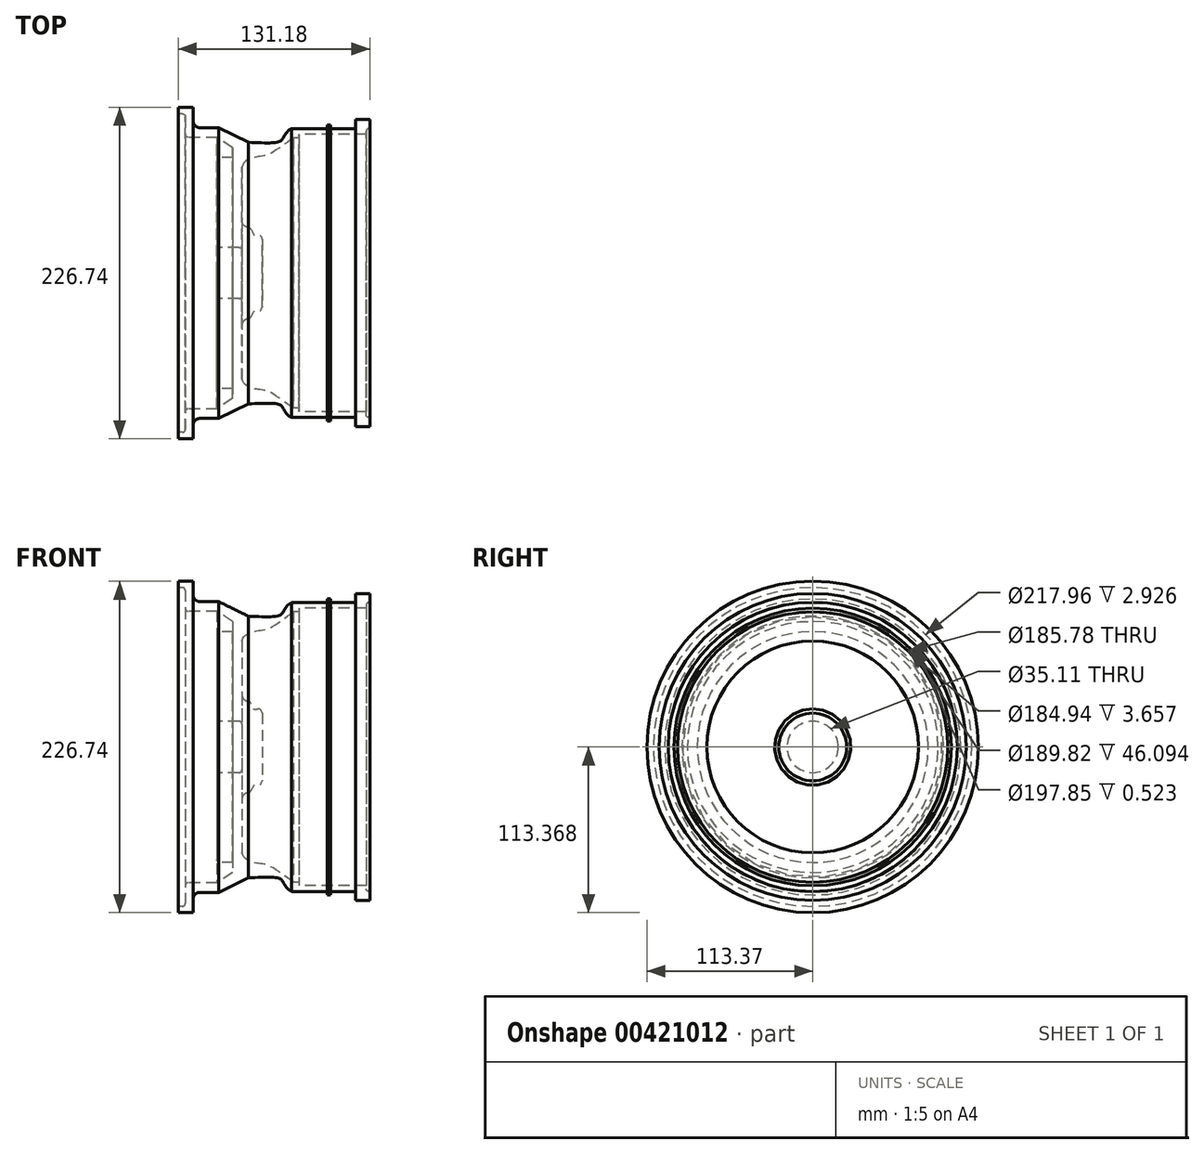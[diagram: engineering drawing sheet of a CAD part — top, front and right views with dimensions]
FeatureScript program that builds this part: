
annotation { "Feature Type Name" : "Feature", "Feature Type Description" : "" }
export const myFeature = defineFeature(function(context is Context, id is Id, definition is map)
    precondition{}
    {
        {
            var Q0;
            Q0=qCreatedBy(makeId("Front.planeOp"),FACE);
            var sketch = newSketch(context, id + "F0", { "sketchPlane" : qUnion([Q0])});
            skLineSegment(sketch, "E0", {"start": v(-61.95, 63.46) * mm, "end": v(-61.95, 59.07) * mm});
            skLineSegment(sketch, "E1", {"start": v(-61.95, 59.07) * mm, "end": v(-59.03, 59.07) * mm});
            skLineSegment(sketch, "E2", {"start": v(-57.07, 57.12) * mm, "end": v(-57.07, 44.93) * mm});
            skPoint(sketch, "E3.visualSharp", {"position": v(-57.07, 59.07) * mm});
            skArc(sketch, "E3.filletArc", {"start": v(-57.07, 57.12) * mm, "mid": v(-57.65, 58.5) * mm, "end": v(-59.03, 59.07) * mm});
            skLineSegment(sketch, "E4", {"start": v(-55.12, 42.98) * mm, "end": v(-35.38, 42.98) * mm});
            skPoint(sketch, "E5.visualSharp", {"position": v(-57.07, 42.98) * mm});
            skArc(sketch, "E5.filletArc", {"start": v(-57.07, 44.93) * mm, "mid": v(-56.5, 43.55) * mm, "end": v(-55.12, 42.98) * mm});
            skLineSegment(sketch, "E6", {"start": v(-35.38, 42.98) * mm, "end": v(-24.65, 35.9) * mm});
            skLineSegment(sketch, "E7", {"start": v(-24.65, 35.9) * mm, "end": v(-24.65, 29.08) * mm});
            skLineSegment(sketch, "E8", {"start": v(-24.65, 29.08) * mm, "end": v(-33.43, 29.08) * mm});
            skLineSegment(sketch, "E9", {"start": v(-35.38, 27.13) * mm, "end": v(-35.38, -32.36) * mm});
            skLineSegment(sketch, "E10", {"start": v(-35.38, -32.36) * mm, "end": v(-20.26, -32.36) * mm});
            skLineSegment(sketch, "E11", {"start": v(-18.3, -34.3) * mm, "end": v(-18.3, -49.91) * mm});
            skLineSegment(sketch, "E12", {"start": v(-18.3, -49.91) * mm, "end": v(-4.52, -49.91) * mm});
            skLineSegment(sketch, "E13", {"start": v(-4.52, -49.91) * mm, "end": v(-4.52, -26.75) * mm});
            skPoint(sketch, "E14.visualSharp", {"position": v(-35.38, 29.08) * mm});
            skArc(sketch, "E14.filletArc", {"start": v(-33.43, 29.08) * mm, "mid": v(-34.8, 28.5) * mm, "end": v(-35.38, 27.13) * mm});
            skPoint(sketch, "E15.visualSharp", {"position": v(-18.3, -32.36) * mm});
            skArc(sketch, "E15.filletArc", {"start": v(-18.3, -34.3) * mm, "mid": v(-18.88, -32.93) * mm, "end": v(-20.26, -32.36) * mm});
            skFitSpline(sketch, "E16", {"points": [v(-4.52, -26.75) * mm, v(-6.6, -23.82) * mm, v(-9.53, -24.31) * mm, v(-12.46, -19.44) * mm, v(-18.3, -18.95) * mm], "startDerivative": vector(-6.91, 20.58) * mm, "endDerivative": vector(-29.24, -4.58) * mm});
            skLineSegment(sketch, "E17", {"start": v(-18.3, -14.09) * mm, "end": v(-18.3, 22.5) * mm});
            skArc(sketch, "E18.filletArc", {"start": v(-18.3, -14.09) * mm, "mid": v(-17.16, -17.09) * mm, "end": v(-14.3, -18.55) * mm});
            skFitSpline(sketch, "E19", {"points": [v(-18.3, 22.5) * mm, v(-16.36, 26.16) * mm, v(-8.07, 29.57) * mm, v(0, 31.28) * mm, v(17, 42.56) * mm], "startDerivative": vector(6.68, 22.89) * mm, "endDerivative": vector(47.85, 31.3) * mm});
            skLineSegment(sketch, "E20", {"start": v(17, 42.56) * mm, "end": v(20.66, 42.56) * mm});
            skLineSegment(sketch, "E21", {"start": v(20.66, 42.56) * mm, "end": v(20.66, 45) * mm});
            skLineSegment(sketch, "E22", {"start": v(20.66, 45) * mm, "end": v(66.75, 45) * mm});
            skLineSegment(sketch, "E23", {"start": v(66.75, 45) * mm, "end": v(66.75, 47.06) * mm});
            skLineSegment(sketch, "E24", {"start": v(68.7, 49.01) * mm, "end": v(69.23, 49.01) * mm});
            skLineSegment(sketch, "E25", {"start": v(69.23, 49.01) * mm, "end": v(69.23, 55.07) * mm});
            skLineSegment(sketch, "E26", {"start": v(69.23, 55.07) * mm, "end": v(59.32, 55.07) * mm});
            skLineSegment(sketch, "E27", {"start": v(59.32, 55.07) * mm, "end": v(59.32, 48.9) * mm});
            skLineSegment(sketch, "E28", {"start": v(59.32, 48.9) * mm, "end": v(42.2, 48.9) * mm});
            skLineSegment(sketch, "E29", {"start": v(42.2, 48.9) * mm, "end": v(42.2, 51.35) * mm});
            skLineSegment(sketch, "E30", {"start": v(42.2, 51.35) * mm, "end": v(40.16, 51.35) * mm});
            skLineSegment(sketch, "E31", {"start": v(40.16, 51.35) * mm, "end": v(40.16, 48.9) * mm});
            skLineSegment(sketch, "E32", {"start": v(40.16, 48.9) * mm, "end": v(15.53, 48.9) * mm});
            skFitSpline(sketch, "E33", {"points": [v(15.53, 48.9) * mm, v(10.46, 43.47) * mm, v(7.29, 40.05) * mm, v(-13.9, 39.56) * mm], "startDerivative": vector(-23.57, -8.95) * mm, "endDerivative": vector(-53.39, 2.2) * mm});
            skLineSegment(sketch, "E34", {"start": v(-13.9, 39.56) * mm, "end": v(-34.37, 49.56) * mm});
            skLineSegment(sketch, "E35", {"start": v(-34.37, 49.56) * mm, "end": v(-47.2, 49.56) * mm});
            skLineSegment(sketch, "E36", {"start": v(-51.69, 54.05) * mm, "end": v(-51.69, 63.46) * mm});
            skLineSegment(sketch, "E37", {"start": v(-51.69, 63.46) * mm, "end": v(-61.95, 63.46) * mm});
            skPoint(sketch, "E38.visualSharp", {"position": v(-51.69, 49.56) * mm});
            skArc(sketch, "E38.filletArc", {"start": v(-51.69, 54.05) * mm, "mid": v(-50.37, 50.87) * mm, "end": v(-47.2, 49.56) * mm});
            skPoint(sketch, "E39.visualSharp", {"position": v(66.75, 49.01) * mm});
            skArc(sketch, "E39.filletArc", {"start": v(68.7, 49.01) * mm, "mid": v(67.32, 48.44) * mm, "end": v(66.75, 47.06) * mm});
            skSolve(sketch);
        }
        {
            var Q0;
            Q0=makeQuery(id+"F0.imprint","IMPRINT",FACE,{"disambiguationData":[TD([[makeQuery(id+"F0.imprint","IMPRINT",EDGE,{"derivedFrom":sQuery(id+"F0.wireOp",EDGE,"E0")}),1.0]])]});
            var Q1;
            Q1=sQuery(id+"F0.wireOp",EDGE,"E12");
            revolve(context, id + "F1", {"entities" : qUnion([Q0]), "axis" : qUnion([Q1]), "revolveType" : RevolveType.FULL});
        }
    });
